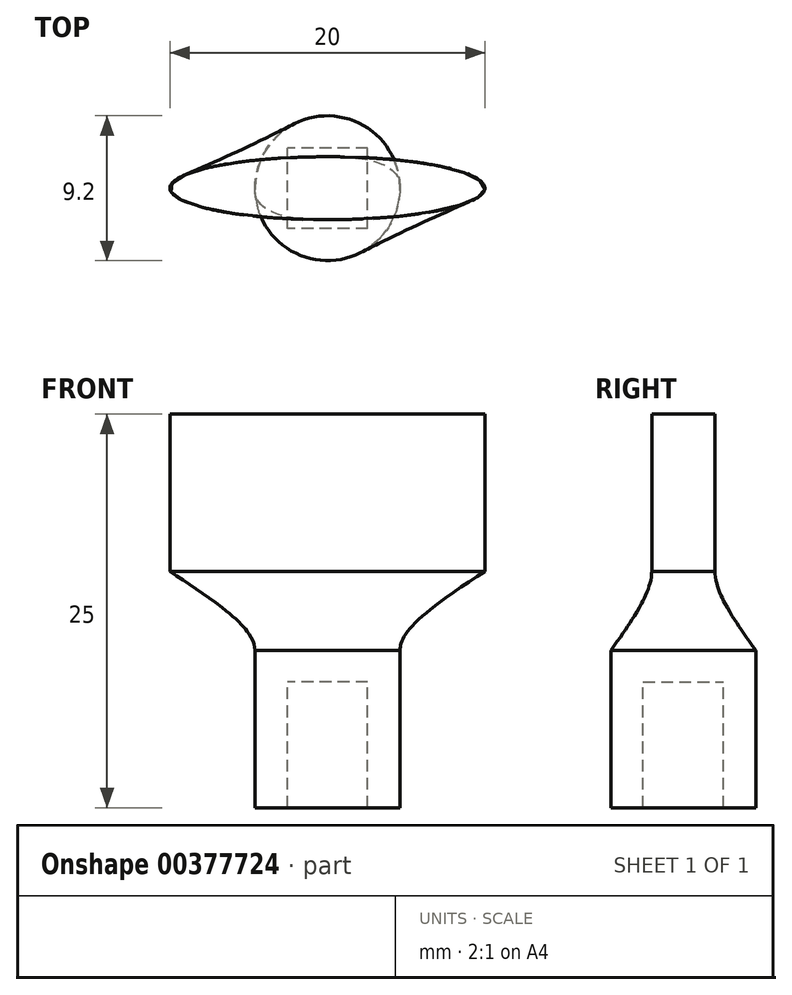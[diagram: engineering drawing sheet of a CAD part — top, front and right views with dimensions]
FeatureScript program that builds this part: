
annotation { "Feature Type Name" : "Feature", "Feature Type Description" : "" }
export const myFeature = defineFeature(function(context is Context, id is Id, definition is map)
    precondition{}
    {
        {
            var Q0;
            Q0=qCreatedBy(makeId("Top.planeOp"),FACE);
            var sketch = newSketch(context, id + "F0", { "sketchPlane" : qUnion([Q0])});
            skLineSegment(sketch, "E0.bottom", {"start": v(2.55, -2.55) * mm, "end": v(-2.55, -2.55) * mm});
            skLineSegment(sketch, "E0.top", {"start": v(2.55, 2.55) * mm, "end": v(-2.55, 2.55) * mm});
            skLineSegment(sketch, "E0.left", {"start": v(2.55, -2.55) * mm, "end": v(2.55, 2.55) * mm});
            skLineSegment(sketch, "E0.right", {"start": v(-2.55, -2.55) * mm, "end": v(-2.55, 2.55) * mm});
            skPoint(sketch, "E0.middle", {"position": v(0, 0) * mm});
            skCircle(sketch, "E1", {"center": v(0, 0) * mm, "radius": 4.6 * mm});
            skSolve(sketch);
        }
        {
            var Q0;
            Q0=makeQuery(id+"F0.imprint","IMPRINT",FACE,{"disambiguationData":[TD([[makeQuery(id+"F0.imprint","IMPRINT",EDGE,{"derivedFrom":sQuery(id+"F0.wireOp",EDGE,"E0.bottom")}),1.0]])]});
            extrude(context, id + "F1", {"entities" : qUnion([Q0]), "oppositeDirection" : true, "depth" : 8 * mm});
        }
        {
            var Q0;
            Q0=makeQuery(id+"F0.imprint","IMPRINT",FACE,{"disambiguationData":[TD([[makeQuery(id+"F0.imprint","IMPRINT",EDGE,{"derivedFrom":sQuery(id+"F0.wireOp",EDGE,"E0.bottom")}),-1.0]])]});
            var Q1;
            Q1=makeQuery(id+"F0.imprint","IMPRINT",FACE,{"disambiguationData":[TD([[makeQuery(id+"F0.imprint","IMPRINT",EDGE,{"derivedFrom":sQuery(id+"F0.wireOp",EDGE,"E0.bottom")}),1.0]])]});
            extrude(context, id + "F2", {"entities" : qUnion([Q0, Q1]), "operationType" : NewBodyOperationType.ADD, "depth" : 2 * mm});
        }
        {
            var Q0;
            Q0=makeQuery(id+"F2.opExtrude","CAP_FACE",FACE,{"disambiguationData":[OSD([sQuery(id+"F0.wireOp",EDGE,"E1")])],"isStart":false});
            cPlane(context, id + "F3", {"entities" : qUnion([Q0]), "cplaneType" : CPlaneType.OFFSET, "offset" : 5 * mm, "width" : 150 * mm, "height" : 150 * mm});
        }
        {
            var Q0;
            Q0=qCreatedBy(id+"F3.planeOp",FACE);
            var sketch = newSketch(context, id + "F4", { "sketchPlane" : qUnion([Q0])});
            skEllipse(sketch, "E2", {"center": v(0, 0) * mm, "majorRadius": 10 * mm, "minorRadius": 2 * mm, "majorAxis": v(1, 0)});
            skSolve(sketch);
        }
        {
            var Q1;
            Q1=makeQuery(id+"F2.opExtrude","CAP_FACE",FACE,{"disambiguationData":[OSD([sQuery(id+"F0.wireOp",EDGE,"E1")])],"isStart":false});
            var Q2;
            Q2=makeQuery(id+"F4.imprint","IMPRINT",FACE,{"disambiguationData":[TD([[makeQuery(id+"F4.imprint","IMPRINT",EDGE,{"derivedFrom":sQuery(id+"F4.wireOp",EDGE,"E2")}),1.0]])]});
            loft(context, id + "F5", {"operationType" : NewBodyOperationType.ADD, "sheetProfilesArray" : [{ "sheetProfileEntities" : qUnion([Q1]) }, { "sheetProfileEntities" : qUnion([Q2]) }]});
        }
        {
            var Q0;
            Q0=makeQuery(id+"F5.opLoft","CAP_FACE",FACE,{"disambiguationData":[OSD([makeQuery(id+"F4.imprint","IMPRINT",FACE,{"disambiguationData":[TD([[makeQuery(id+"F4.imprint","IMPRINT",EDGE,{"derivedFrom":sQuery(id+"F4.wireOp",EDGE,"E2")}),1.0]])]})])],"isStart":true});
            extrude(context, id + "F6", {"entities" : qUnion([Q0]), "operationType" : NewBodyOperationType.ADD, "depth" : 10 * mm});
        }
    });
